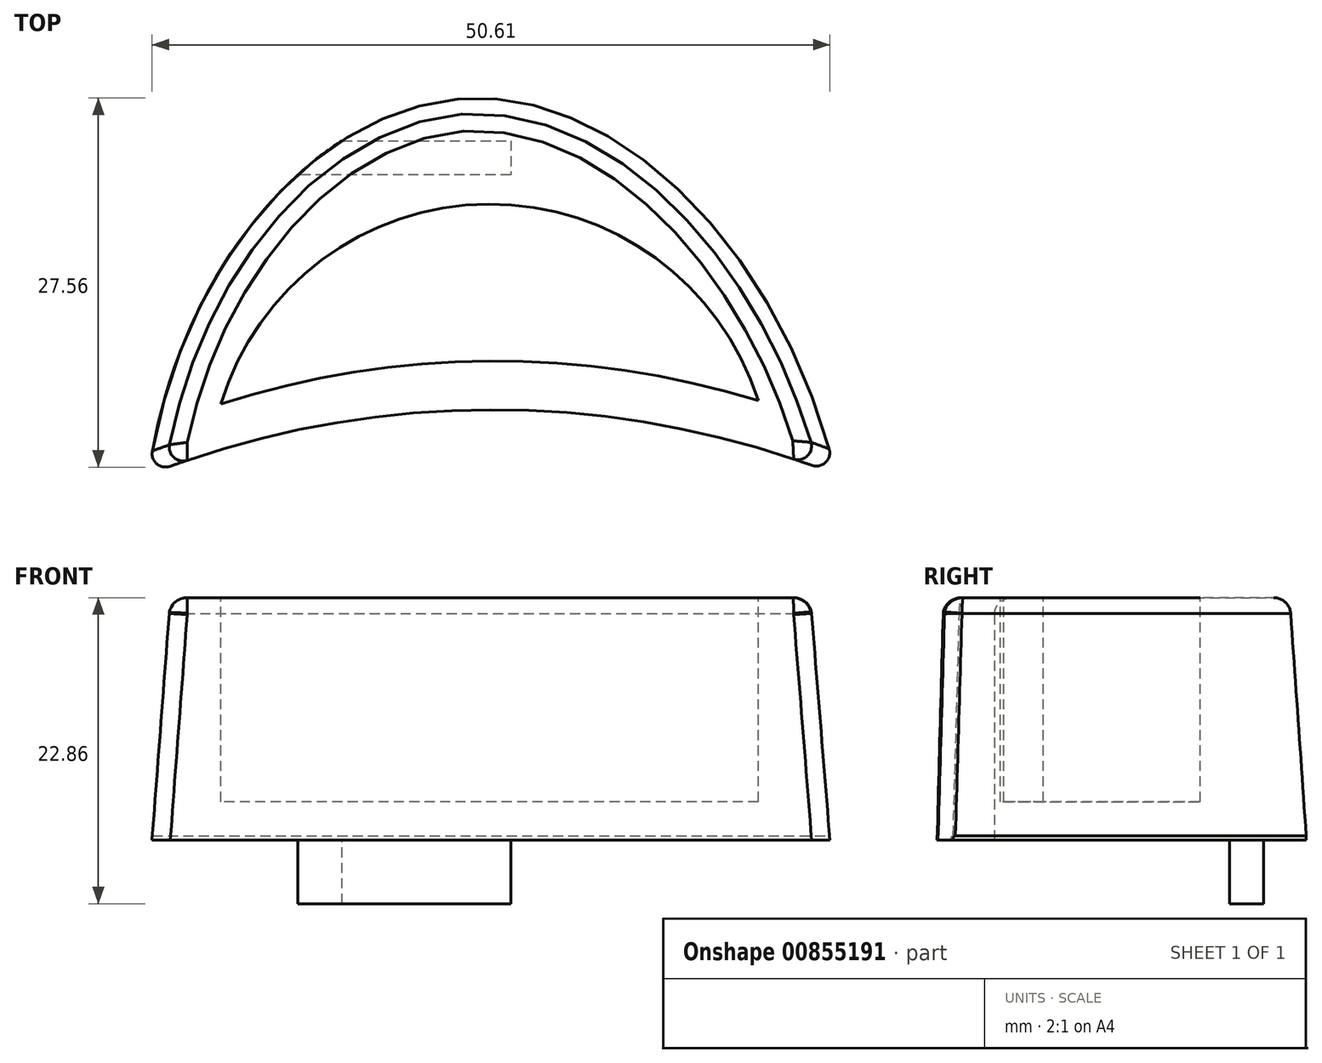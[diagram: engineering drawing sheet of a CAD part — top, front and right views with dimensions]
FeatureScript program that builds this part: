
annotation { "Feature Type Name" : "Feature", "Feature Type Description" : "" }
export const myFeature = defineFeature(function(context is Context, id is Id, definition is map)
    precondition{}
    {
        {
            var Q0;
            Q0=qCreatedBy(makeId("Top.planeOp"),FACE);
            var sketch = newSketch(context, id + "F0", { "sketchPlane" : qUnion([Q0])});
            skArc(sketch, "E0", {"start": v(53.97, 0) * mm, "mid": v(26.99, 5.08) * mm, "end": v(0, 0) * mm});
            skFitSpline(sketch, "E1", {"points": [v(0, 0) * mm, v(25.26, 29.57) * mm, v(53.97, 0) * mm], "startDerivative": vector(13.72, 100.65) * mm, "endDerivative": vector(24.23, -102.26) * mm});
            skSolve(sketch);
        }
        {
            var Q0;
            Q0=makeQuery(id+"F0.imprint","IMPRINT",FACE,{"disambiguationData":[TD([[makeQuery(id+"F0.imprint","IMPRINT",EDGE,{"derivedFrom":sQuery(id+"F0.wireOp",EDGE,"E0")}),-1.0]])]});
            extrude(context, id + "F1", {"entities" : qUnion([Q0]), "depth" : 19.05 * mm, "offsetDistance" : 25.4 * mm});
        }
        {
            var Q0;
            Q0=makeQuery(id+"F1.opExtrude","SWEPT_BODY",BODY,{"disambiguationData":[OSD([sQuery(id+"F0.wireOp",EDGE,"E0"),sQuery(id+"F0.wireOp",EDGE,"E1")])]});
            var Q1;
            Q1=qCreatedBy(makeId("Origin.pointOp"),VERTEX);
            transform(context, id + "F2", {"entities" : qUnion([Q0]), "transformType" : TransformType.SCALE_UNIFORMLY, "scale" : .95, "scalePoint" : qUnion([Q1]), "makeCopy" : false});
        }
        {
            var Q0;
            Q0=makeQuery(id+"F1.opExtrude","CAP_FACE",FACE,{"disambiguationData":[OSD([sQuery(id+"F0.wireOp",EDGE,"E0"),sQuery(id+"F0.wireOp",EDGE,"E1")])],"isStart":true});
            var sketch = newSketch(context, id + "F3", { "sketchPlane" : qUnion([Q0])});
            skLineSegment(sketch, "E2", {"start": v(14.43, -24.91) * mm, "end": v(27.02, -24.91) * mm});
            skLineSegment(sketch, "E3", {"start": v(27.02, -24.91) * mm, "end": v(27.02, -22.37) * mm});
            skLineSegment(sketch, "E4", {"start": v(27.02, -22.37) * mm, "end": v(11.13, -22.37) * mm});
            skSolve(sketch);
        }
        {
            var Q0;
            {var subQ0=sQuery(id+"F3.wireOp",EDGE,"E2");Q0=makeQuery(id+"F3.imprint","IMPRINT",FACE,{"disambiguationData":[TD([[makeQuery(id+"F3.imprint","IMPRINT",EDGE,{"derivedFrom":subQ0}),1.0]])]});}
            extrude(context, id + "F4", {"entities" : qUnion([Q0]), "operationType" : NewBodyOperationType.ADD, "depth" : 4.76 * mm, "offsetDistance" : 25.4 * mm});
        }
        {
            var Q0;
            Q0=makeQuery(id+"F1.opExtrude","CAP_EDGE",EDGE,{"disambiguationData":[OSD([sQuery(id+"F0.wireOp",EDGE,"E1")])],"isStart":false});
            chamfer(context, id + "F5", {"entities" : qUnion([Q0]), "chamferType" : ChamferType.OFFSET_ANGLE, "width" : 17.78 * mm, "oppositeDirection" : false, "angle" : 4 * degree, "tangentPropagation" : true});
        }
        {
            var Q0;
            Q0=makeQuery(id+"F5.opChamfer","BLEND_EDGE",EDGE,{"disambiguationData":[OD(0.0)],"blendedFrom":[makeQuery(id+"F1.opExtrude","CAP_EDGE",EDGE,{"disambiguationData":[OSD([sQuery(id+"F0.wireOp",EDGE,"E1")])],"isStart":false}),makeQuery(id+"F1.opExtrude","SWEPT_FACE",FACE,{"disambiguationData":[OSD([sQuery(id+"F0.wireOp",EDGE,"E0")])]})],"blendedInto":[makeQuery(id+"F1.opExtrude","SWEPT_FACE",FACE,{"disambiguationData":[OSD([sQuery(id+"F0.wireOp",EDGE,"E0")])]})]});
            var Q1;
            Q1=makeQuery(id+"F5.opChamfer","BLEND_EDGE",EDGE,{"disambiguationData":[OD(1.0)],"blendedFrom":[makeQuery(id+"F1.opExtrude","CAP_EDGE",EDGE,{"disambiguationData":[OSD([sQuery(id+"F0.wireOp",EDGE,"E1")])],"isStart":false}),makeQuery(id+"F1.opExtrude","SWEPT_FACE",FACE,{"disambiguationData":[OSD([sQuery(id+"F0.wireOp",EDGE,"E0")])]})],"blendedInto":[makeQuery(id+"F1.opExtrude","SWEPT_FACE",FACE,{"disambiguationData":[OSD([sQuery(id+"F0.wireOp",EDGE,"E0")])]})]});
            fillet(context, id + "F6", {"entities" : qUnion([Q0, Q1]), "radius" : 1.02 * mm, "tangentPropagation" : true, "allowEdgeOverflow" : false});
        }
        {
            var Q0;
            Q0=makeQuery(id+"F1.opExtrude","CAP_FACE",FACE,{"disambiguationData":[OSD([sQuery(id+"F0.wireOp",EDGE,"E0"),sQuery(id+"F0.wireOp",EDGE,"E1")])],"isStart":false});
            var sketch = newSketch(context, id + "F7", { "sketchPlane" : qUnion([Q0])});
            skArc(sketch, "E5", {"start": v(45.5, 5.5) * mm, "mid": v(25.42, 8.46) * mm, "end": v(5.38, 5.26) * mm});
            skArc(sketch, "E6", {"start": v(45.5, 5.5) * mm, "mid": v(25.34, 20.19) * mm, "end": v(5.38, 5.26) * mm});
            skSolve(sketch);
        }
        {
            var Q0;
            Q0=makeQuery(id+"F7.imprint","IMPRINT",FACE,{"disambiguationData":[TD([[makeQuery(id+"F7.imprint","IMPRINT",EDGE,{"derivedFrom":sQuery(id+"F7.wireOp",EDGE,"E5")}),-1.0]])]});
            extrude(context, id + "F8", {"entities" : qUnion([Q0]), "operationType" : NewBodyOperationType.REMOVE, "oppositeDirection" : true, "depth" : 15.24 * mm, "offsetDistance" : 25.4 * mm});
        }
        {
            var Q0;
            {var subQ0=sQuery(id+"F0.wireOp",EDGE,"E1");Q0=makeQuery(id+"F5.opChamfer","BLEND_EDGE",EDGE,{"blendedFrom":[makeQuery(id+"F1.opExtrude","CAP_EDGE",EDGE,{"disambiguationData":[OSD([subQ0])],"isStart":false}),makeQuery(id+"F1.opExtrude","CAP_FACE",FACE,{"disambiguationData":[OSD([sQuery(id+"F0.wireOp",EDGE,"E0"),subQ0])],"isStart":false})],"blendedInto":[makeQuery(id+"F1.opExtrude","CAP_FACE",FACE,{"disambiguationData":[OSD([sQuery(id+"F0.wireOp",EDGE,"E0"),subQ0])],"isStart":false})]});}
            var Q1;
            Q1=makeQuery(id+"F1.opExtrude","CAP_EDGE",EDGE,{"disambiguationData":[OSD([sQuery(id+"F0.wireOp",EDGE,"E0")])],"isStart":false});
            var Q2;
            {var subQ0=sQuery(id+"F0.wireOp",EDGE,"E1");var subQ1=sQuery(id+"F0.wireOp",EDGE,"E0");Q2=makeQuery(id+"F6.opFillet","BLEND_EDGE",EDGE,{"blendedFrom":[makeQuery(id+"F5.opChamfer","BLEND_EDGE",EDGE,{"disambiguationData":[OD(0.0)],"blendedFrom":[makeQuery(id+"F1.opExtrude","CAP_EDGE",EDGE,{"disambiguationData":[OSD([subQ0])],"isStart":false}),makeQuery(id+"F1.opExtrude","SWEPT_FACE",FACE,{"disambiguationData":[OSD([subQ1])]})],"blendedInto":[makeQuery(id+"F1.opExtrude","SWEPT_FACE",FACE,{"disambiguationData":[OSD([subQ1])]})]}),makeQuery(id+"F1.opExtrude","CAP_FACE",FACE,{"disambiguationData":[OSD([subQ1,subQ0])],"isStart":false})],"blendedInto":[makeQuery(id+"F1.opExtrude","CAP_FACE",FACE,{"disambiguationData":[OSD([subQ1,subQ0])],"isStart":false})]});}
            var Q3;
            {var subQ0=sQuery(id+"F0.wireOp",EDGE,"E1");var subQ1=sQuery(id+"F0.wireOp",EDGE,"E0");Q3=makeQuery(id+"F6.opFillet","BLEND_EDGE",EDGE,{"blendedFrom":[makeQuery(id+"F5.opChamfer","BLEND_EDGE",EDGE,{"disambiguationData":[OD(1.0)],"blendedFrom":[makeQuery(id+"F1.opExtrude","CAP_EDGE",EDGE,{"disambiguationData":[OSD([subQ0])],"isStart":false}),makeQuery(id+"F1.opExtrude","SWEPT_FACE",FACE,{"disambiguationData":[OSD([subQ1])]})],"blendedInto":[makeQuery(id+"F1.opExtrude","SWEPT_FACE",FACE,{"disambiguationData":[OSD([subQ1])]})]}),makeQuery(id+"F1.opExtrude","CAP_FACE",FACE,{"disambiguationData":[OSD([subQ1,subQ0])],"isStart":false})],"blendedInto":[makeQuery(id+"F1.opExtrude","CAP_FACE",FACE,{"disambiguationData":[OSD([subQ1,subQ0])],"isStart":false})]});}
            fillet(context, id + "F9", {"entities" : qUnion([Q0, Q1, Q2, Q3]), "radius" : 1.27 * mm, "tangentPropagation" : true, "allowEdgeOverflow" : false});
        }
    });
